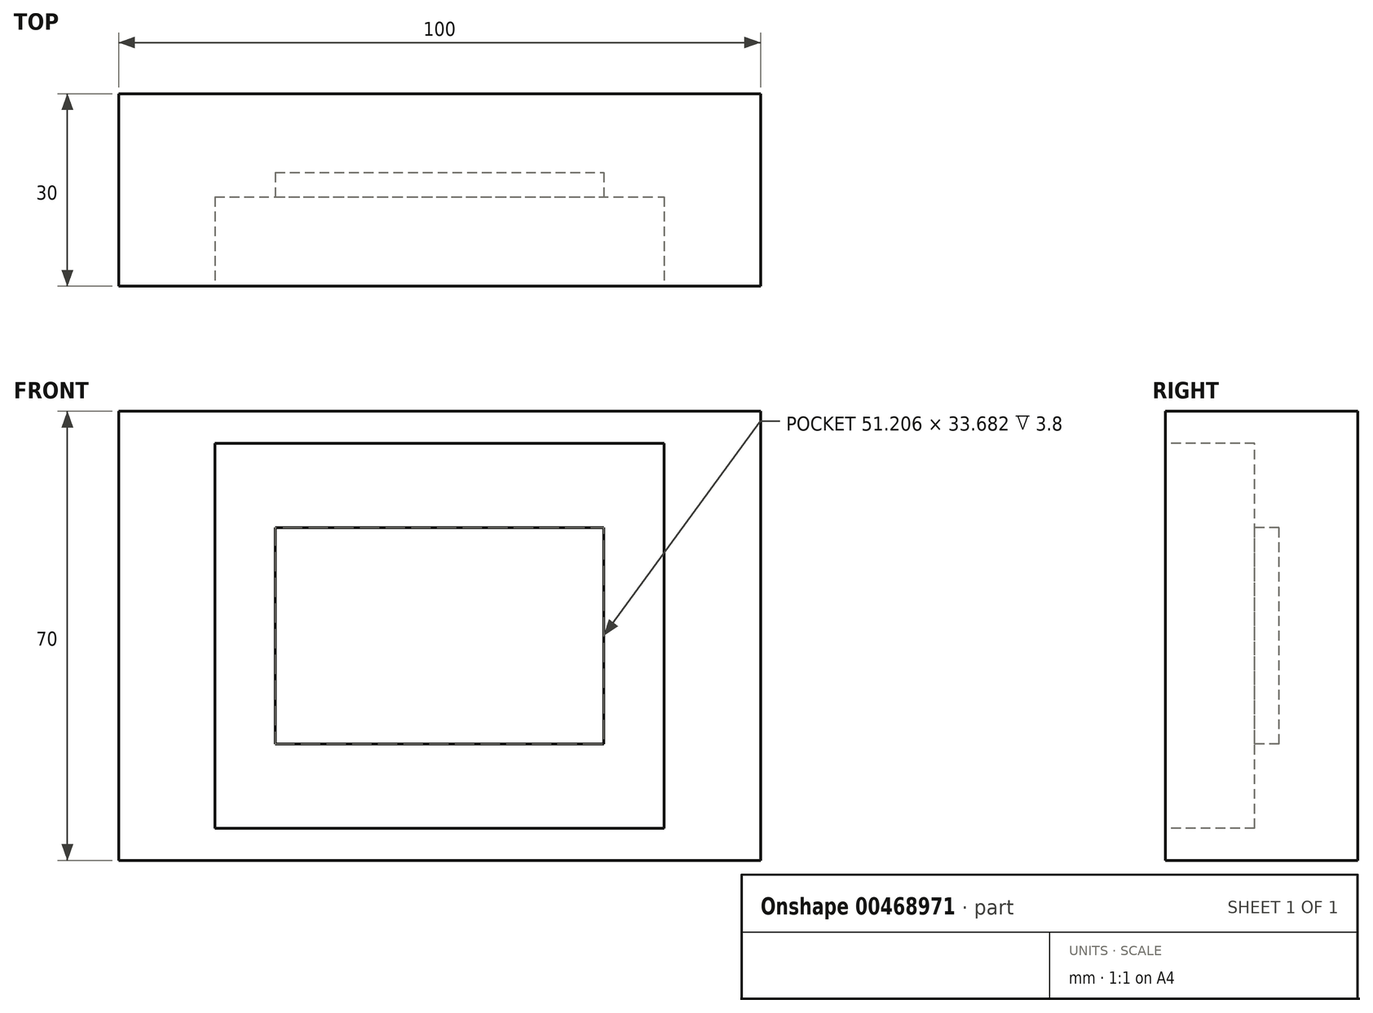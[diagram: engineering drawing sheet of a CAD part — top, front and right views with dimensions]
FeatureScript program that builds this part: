
annotation { "Feature Type Name" : "Feature", "Feature Type Description" : "" }
export const myFeature = defineFeature(function(context is Context, id is Id, definition is map)
    precondition{}
    {
        {
            var Q0;
            Q0=qCreatedBy(makeId("Front.planeOp"),FACE);
            var sketch = newSketch(context, id + "F0", { "sketchPlane" : qUnion([Q0])});
            skLineSegment(sketch, "E0.bottom", {"start": v(50, 35) * mm, "end": v(-50, 35) * mm});
            skLineSegment(sketch, "E0.top", {"start": v(50, -35) * mm, "end": v(-50, -35) * mm});
            skLineSegment(sketch, "E0.left", {"start": v(50, 35) * mm, "end": v(50, -35) * mm});
            skLineSegment(sketch, "E0.right", {"start": v(-50, 35) * mm, "end": v(-50, -35) * mm});
            skPoint(sketch, "E0.middle", {"position": v(0, 0) * mm});
            skSolve(sketch);
        }
        {
            var Q0;
            Q0=makeQuery(id+"F0.imprint","IMPRINT",FACE,{"disambiguationData":[TD([[makeQuery(id+"F0.imprint","IMPRINT",EDGE,{"derivedFrom":sQuery(id+"F0.wireOp",EDGE,"E0.bottom")}),1.0]])]});
            extrude(context, id + "F1", {"entities" : qUnion([Q0]), "depth" : 30 * mm, "offsetDistance" : 25 * mm});
        }
        {
            var Q0;
            Q0=makeQuery(id+"F1.opExtrude","CAP_FACE",FACE,{"disambiguationData":[OSD([sQuery(id+"F0.wireOp",EDGE,"E0.bottom"),sQuery(id+"F0.wireOp",EDGE,"E0.top"),sQuery(id+"F0.wireOp",EDGE,"E0.left"),sQuery(id+"F0.wireOp",EDGE,"E0.right")])],"isStart":false});
            var sketch = newSketch(context, id + "F2", { "sketchPlane" : qUnion([Q0])});
            skLineSegment(sketch, "E1.bottom", {"start": v(-35, -30) * mm, "end": v(35, -30) * mm});
            skLineSegment(sketch, "E1.top", {"start": v(-35, 30) * mm, "end": v(35, 30) * mm});
            skLineSegment(sketch, "E1.left", {"start": v(-35, -30) * mm, "end": v(-35, 30) * mm});
            skLineSegment(sketch, "E1.right", {"start": v(35, -30) * mm, "end": v(35, 30) * mm});
            skPoint(sketch, "E1.middle", {"position": v(0, 0) * mm});
            skSolve(sketch);
        }
        {
            var Q0;
            Q0=makeQuery(id+"F2.imprint","IMPRINT",FACE,{"disambiguationData":[TD([[makeQuery(id+"F2.imprint","IMPRINT",EDGE,{"derivedFrom":sQuery(id+"F2.wireOp",EDGE,"E1.bottom")}),1.0]])]});
            extrude(context, id + "F3", {"entities" : qUnion([Q0]), "operationType" : NewBodyOperationType.REMOVE, "oppositeDirection" : true, "depth" : 13.9 * mm, "offsetDistance" : 25 * mm});
        }
        {
            var Q0;
            Q0=makeQuery(id+"F3.boolean.opBoolean","COPY",FACE,{"derivedFrom":makeQuery(id+"F3.opExtrude","CAP_FACE",FACE,{"disambiguationData":[OSD([sQuery(id+"F2.wireOp",EDGE,"E1.bottom"),sQuery(id+"F2.wireOp",EDGE,"E1.top"),sQuery(id+"F2.wireOp",EDGE,"E1.left"),sQuery(id+"F2.wireOp",EDGE,"E1.right")])],"isStart":false})});
            var sketch = newSketch(context, id + "F4", { "sketchPlane" : qUnion([Q0])});
            skLineSegment(sketch, "E2.bottom", {"start": v(-25.6, -16.84) * mm, "end": v(25.6, -16.84) * mm});
            skLineSegment(sketch, "E2.top", {"start": v(-25.6, 16.84) * mm, "end": v(25.6, 16.84) * mm});
            skLineSegment(sketch, "E2.left", {"start": v(-25.6, -16.84) * mm, "end": v(-25.6, 16.84) * mm});
            skLineSegment(sketch, "E2.right", {"start": v(25.6, -16.84) * mm, "end": v(25.6, 16.84) * mm});
            skPoint(sketch, "E2.middle", {"position": v(0, 0) * mm});
            skSolve(sketch);
        }
        {
            var Q0;
            Q0=makeQuery(id+"F4.imprint","IMPRINT",FACE,{"disambiguationData":[TD([[makeQuery(id+"F4.imprint","IMPRINT",EDGE,{"derivedFrom":sQuery(id+"F4.wireOp",EDGE,"E2.bottom")}),1.0]])]});
            extrude(context, id + "F5", {"entities" : qUnion([Q0]), "operationType" : NewBodyOperationType.REMOVE, "oppositeDirection" : true, "depth" : 3.8 * mm, "offsetDistance" : 25 * mm});
        }
        {
            var Q0;
            Q0=makeQuery(id+"F1.opExtrude","CAP_FACE",FACE,{"disambiguationData":[OSD([sQuery(id+"F0.wireOp",EDGE,"E0.bottom"),sQuery(id+"F0.wireOp",EDGE,"E0.top"),sQuery(id+"F0.wireOp",EDGE,"E0.left"),sQuery(id+"F0.wireOp",EDGE,"E0.right")])],"isStart":false});
            cPlane(context, id + "F6", {"entities" : qUnion([Q0]), "cplaneType" : CPlaneType.OFFSET, "offset" : 67.6 * mm, "width" : 150 * mm, "height" : 150 * mm});
        }
    });
